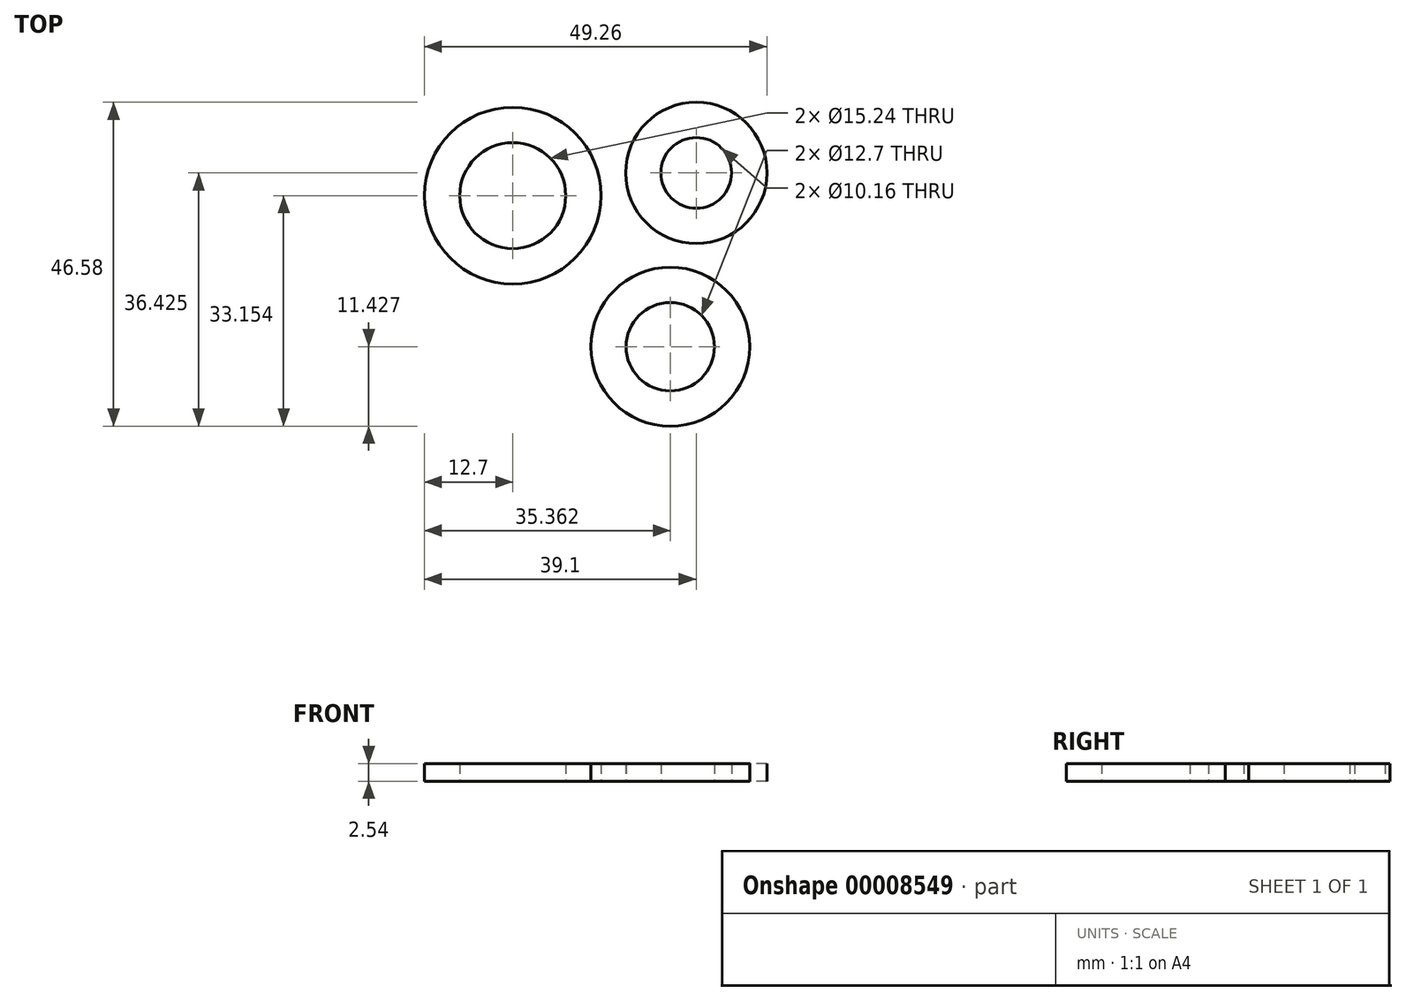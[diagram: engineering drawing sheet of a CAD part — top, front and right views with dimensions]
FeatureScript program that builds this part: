
annotation { "Feature Type Name" : "Feature", "Feature Type Description" : "" }
export const myFeature = defineFeature(function(context is Context, id is Id, definition is map)
    precondition{}
    {
        {
            var Q0;
            Q0=qCreatedBy(makeId("Top.planeOp"),FACE);
            var sketch = newSketch(context, id + "F0", { "sketchPlane" : qUnion([Q0])});
            skCircle(sketch, "E0", {"center": v(-26.4, 13.78) * mm, "radius": 12.7 * mm});
            skCircle(sketch, "E1", {"center": v(0, 17.05) * mm, "radius": 10.16 * mm});
            skCircle(sketch, "E2", {"center": v(-3.74, -7.94) * mm, "radius": 11.43 * mm});
            skCircle(sketch, "E3", {"center": v(-26.4, 13.78) * mm, "radius": 7.62 * mm});
            skCircle(sketch, "E4", {"center": v(-3.74, -7.94) * mm, "radius": 6.35 * mm});
            skCircle(sketch, "E5", {"center": v(0, 17.05) * mm, "radius": 5.08 * mm});
            skSolve(sketch);
        }
        {
            var Q0;
            Q0 = qSketchRegion(id + "F0", true);
            extrude(context, id + "F1", {"entities" : qUnion([Q0]), "depth" : 2.54 * mm});
        }
    });
